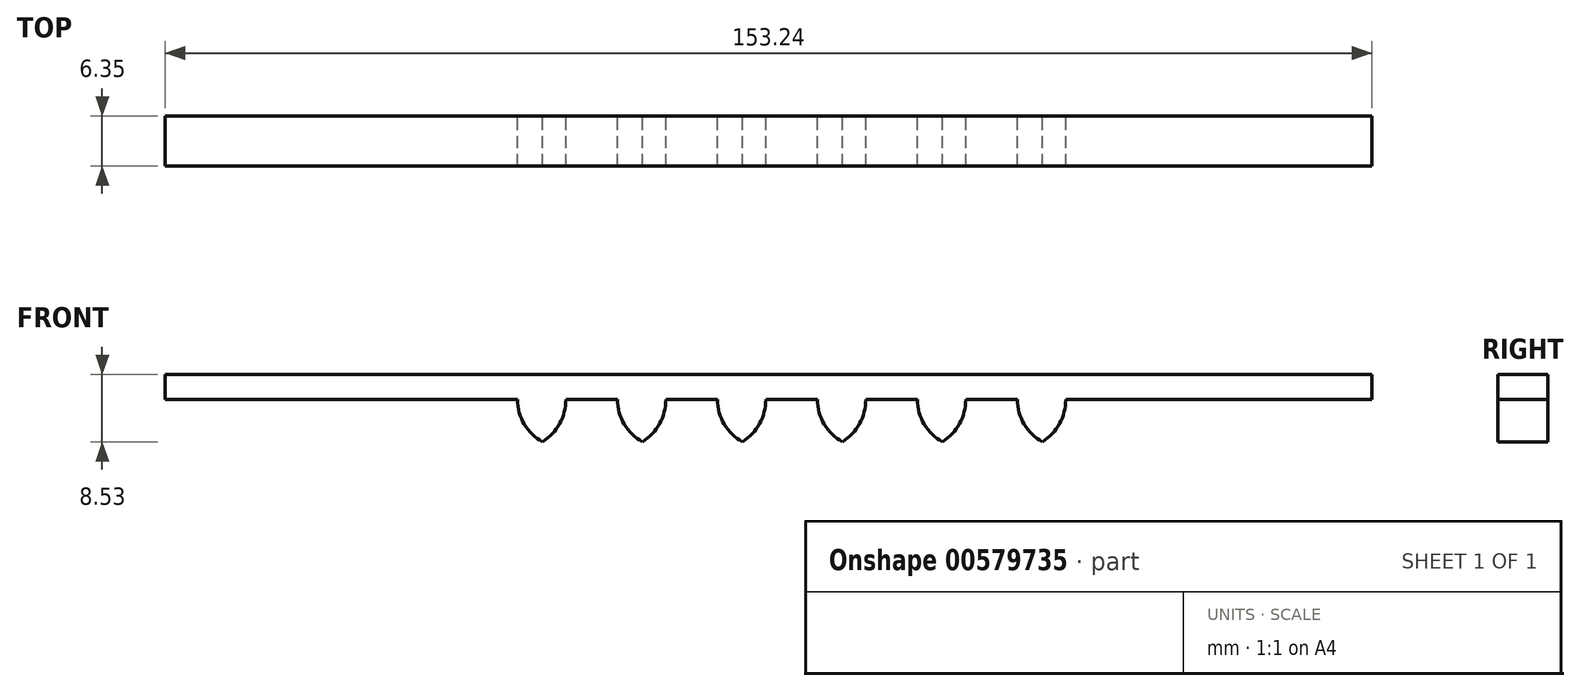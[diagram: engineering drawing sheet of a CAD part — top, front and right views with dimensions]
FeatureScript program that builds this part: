
annotation { "Feature Type Name" : "Feature", "Feature Type Description" : "" }
export const myFeature = defineFeature(function(context is Context, id is Id, definition is map)
    precondition{}
    {
        {
            var Q0;
            Q0=qCreatedBy(makeId("Front.planeOp"),FACE);
            var sketch = newSketch(context, id + "F0", { "sketchPlane" : qUnion([Q0])});
            skLineSegment(sketch, "E0.bottom", {"start": v(-100.17, 36.3) * mm, "end": v(-88.52, 36.3) * mm});
            skArc(sketch, "E1.1.0.0", {"start": v(-85.35, 30.93) * mm, "mid": v(-83.17, 33.23) * mm, "end": v(-82.38, 36.3) * mm});
            skArc(sketch, "E1.1.0.1", {"start": v(-88.52, 36.3) * mm, "mid": v(-87.67, 33.18) * mm, "end": v(-85.35, 30.93) * mm});
            skArc(sketch, "E1.3.0.0", {"start": v(-72.65, 30.93) * mm, "mid": v(-70.47, 33.23) * mm, "end": v(-69.68, 36.3) * mm});
            skArc(sketch, "E1.3.0.1", {"start": v(-75.82, 36.3) * mm, "mid": v(-74.97, 33.18) * mm, "end": v(-72.65, 30.93) * mm});
            skArc(sketch, "E1.5.0.0", {"start": v(-59.95, 30.93) * mm, "mid": v(-57.77, 33.23) * mm, "end": v(-56.98, 36.3) * mm});
            skArc(sketch, "E1.5.0.1", {"start": v(-63.12, 36.3) * mm, "mid": v(-62.27, 33.18) * mm, "end": v(-59.95, 30.93) * mm});
            skArc(sketch, "E1.7.0.0", {"start": v(-47.25, 30.93) * mm, "mid": v(-45.07, 33.23) * mm, "end": v(-44.28, 36.3) * mm});
            skArc(sketch, "E1.7.0.1", {"start": v(-50.42, 36.3) * mm, "mid": v(-49.57, 33.18) * mm, "end": v(-47.25, 30.93) * mm});
            skArc(sketch, "E1.9.0.0", {"start": v(-34.55, 30.93) * mm, "mid": v(-32.37, 33.23) * mm, "end": v(-31.58, 36.3) * mm});
            skArc(sketch, "E1.9.0.1", {"start": v(-37.72, 36.3) * mm, "mid": v(-36.87, 33.18) * mm, "end": v(-34.55, 30.93) * mm});
            skArc(sketch, "E1.11.0.0", {"start": v(-21.85, 30.93) * mm, "mid": v(-19.67, 33.23) * mm, "end": v(-18.88, 36.3) * mm});
            skArc(sketch, "E1.11.0.1", {"start": v(-25.02, 36.3) * mm, "mid": v(-24.17, 33.18) * mm, "end": v(-21.85, 30.93) * mm});
            skLineSegment(sketch, "E1.direction1", {"start": v(-91.7, 30.93) * mm, "end": v(-85.35, 30.93) * mm, "construction": true});
            skLineSegment(sketch, "E2.bottom", {"start": v(-107, 39.46) * mm, "end": v(1.43, 39.46) * mm});
            skLineSegment(sketch, "E3", {"start": v(-100.17, 36.3) * mm, "end": v(-117.13, 36.3) * mm});
            skLineSegment(sketch, "E4", {"start": v(-120.95, 39.46) * mm, "end": v(-107, 39.46) * mm});
            skLineSegment(sketch, "E5", {"start": v(1.43, 39.46) * mm, "end": v(6.42, 39.46) * mm});
            skLineSegment(sketch, "E6", {"start": v(-120.95, 39.46) * mm, "end": v(-133.26, 39.46) * mm});
            skLineSegment(sketch, "E7", {"start": v(-133.26, 39.46) * mm, "end": v(-133.26, 36.3) * mm});
            skLineSegment(sketch, "E8", {"start": v(-117.13, 36.3) * mm, "end": v(-127.73, 36.3) * mm});
            skLineSegment(sketch, "E9", {"start": v(19.98, 36.3) * mm, "end": v(19.98, 39.46) * mm});
            skLineSegment(sketch, "E10", {"start": v(19.98, 39.46) * mm, "end": v(19.98, 36.3) * mm});
            skLineSegment(sketch, "E11", {"start": v(6.42, 39.46) * mm, "end": v(19.98, 39.46) * mm});
            skLineSegment(sketch, "E12", {"start": v(1.43, 36.3) * mm, "end": v(15.68, 36.3) * mm});
            skLineSegment(sketch, "E13.trimOffspring", {"start": v(-82.38, 36.3) * mm, "end": v(-75.82, 36.3) * mm});
            skLineSegment(sketch, "E14.trimOffspring", {"start": v(-69.68, 36.3) * mm, "end": v(-63.12, 36.3) * mm});
            skLineSegment(sketch, "E15.trimOffspring", {"start": v(-56.98, 36.3) * mm, "end": v(-50.42, 36.3) * mm});
            skLineSegment(sketch, "E16.trimOffspring", {"start": v(-44.28, 36.3) * mm, "end": v(-37.72, 36.3) * mm});
            skLineSegment(sketch, "E17.trimOffspring", {"start": v(-31.58, 36.3) * mm, "end": v(-25.02, 36.3) * mm});
            skLineSegment(sketch, "E18.trimOffspring", {"start": v(-18.88, 36.3) * mm, "end": v(1.43, 36.3) * mm});
            skLineSegment(sketch, "E19", {"start": v(-127.73, 36.3) * mm, "end": v(-133.26, 36.3) * mm});
            skLineSegment(sketch, "E20", {"start": v(-133.26, 36.3) * mm, "end": v(19.98, 36.3) * mm});
            skArc(sketch, "E21", {"start": v(28.32, 23.56) * mm, "mid": v(28.4, 21.92) * mm, "end": v(28.6, 20.28) * mm});
            skArc(sketch, "E22", {"start": v(29.49, 30.12) * mm, "mid": v(26.05, 29.83) * mm, "end": v(23.22, 27.85) * mm});
            skArc(sketch, "E23", {"start": v(23.22, 27.85) * mm, "mid": v(25.2, 25.03) * mm, "end": v(28.32, 23.56) * mm});
            skArc(sketch, "E24.1.0", {"start": v(28.66, 20.3) * mm, "mid": v(25.83, 18.33) * mm, "end": v(24.37, 15.2) * mm});
            skArc(sketch, "E24.1.1", {"start": v(24.37, 15.2) * mm, "mid": v(27.5, 13.74) * mm, "end": v(30.93, 14.04) * mm});
            skArc(sketch, "E24.2.0", {"start": v(32.85, 11.38) * mm, "mid": v(31.39, 8.26) * mm, "end": v(31.68, 4.82) * mm});
            skArc(sketch, "E24.2.1", {"start": v(31.68, 4.82) * mm, "mid": v(35.12, 5.12) * mm, "end": v(37.95, 7.1) * mm});
            skArc(sketch, "E24.3.0", {"start": v(40.94, 5.75) * mm, "mid": v(41.24, 2.32) * mm, "end": v(43.21, -0.5) * mm});
            skArc(sketch, "E24.3.1", {"start": v(43.21, -0.5) * mm, "mid": v(46.04, 1.47) * mm, "end": v(47.5, 4.59) * mm});
            skArc(sketch, "E24.4.0", {"start": v(50.76, 4.92) * mm, "mid": v(52.74, 2.1) * mm, "end": v(55.86, 0.64) * mm});
            skArc(sketch, "E24.4.1", {"start": v(55.86, 0.64) * mm, "mid": v(57.32, 3.76) * mm, "end": v(57.02, 7.2) * mm});
            skArc(sketch, "E24.5.0", {"start": v(59.68, 9.12) * mm, "mid": v(62.8, 7.66) * mm, "end": v(66.24, 7.95) * mm});
            skArc(sketch, "E24.5.1", {"start": v(66.24, 7.95) * mm, "mid": v(65.94, 11.39) * mm, "end": v(63.97, 14.21) * mm});
            skArc(sketch, "E24.6.0", {"start": v(65.3, 17.2) * mm, "mid": v(65.32, 17.2) * mm, "end": v(65.33, 17.2) * mm});
            skPoint(sketch, "E24.center", {"position": v(47.4, 23.67) * mm});
            skPoint(sketch, "E24.11.0.end.orphan", {"position": v(28.56, 39.38) * mm});
            skPoint(sketch, "E24.10.0.end.orphan", {"position": v(38.94, 46.7) * mm});
            skPoint(sketch, "E25.orphan", {"position": v(71.57, 19.48) * mm});
            skArc(sketch, "E26.trimOffspring", {"start": v(30.88, 14.02) * mm, "mid": v(31.78, 12.62) * mm, "end": v(32.79, 11.3) * mm});
            skArc(sketch, "E27.trimOffspring", {"start": v(37.9, 7.04) * mm, "mid": v(39.38, 6.27) * mm, "end": v(40.92, 5.64) * mm});
            skArc(sketch, "E28.trimOffspring", {"start": v(47.49, 4.51) * mm, "mid": v(49.15, 4.6) * mm, "end": v(50.8, 4.82) * mm});
            skArc(sketch, "E29.trimOffspring", {"start": v(57.04, 7.15) * mm, "mid": v(58.43, 8.05) * mm, "end": v(59.74, 9.07) * mm});
            skArc(sketch, "E30.trimOffspring", {"start": v(63.97, 14.21) * mm, "mid": v(55.35, 40.86) * mm, "end": v(29.49, 30.12) * mm});
            skLineSegment(sketch, "E31.top", {"start": v(-105.22, 19.73) * mm, "end": v(-99.92, 19.73) * mm});
            skArc(sketch, "E32.MirrorCS", {"start": v(-99.92, 19.73) * mm, "mid": v(-99.07, 22.84) * mm, "end": v(-96.75, 25.1) * mm});
            skArc(sketch, "E33.MirrorCS", {"start": v(-96.75, 25.1) * mm, "mid": v(-94.58, 22.8) * mm, "end": v(-93.79, 19.73) * mm});
            skArc(sketch, "E34.MirrorCS", {"start": v(-87.22, 19.73) * mm, "mid": v(-86.37, 22.84) * mm, "end": v(-84.05, 25.1) * mm});
            skArc(sketch, "E35.MirrorCS", {"start": v(-84.05, 25.1) * mm, "mid": v(-81.88, 22.8) * mm, "end": v(-81.09, 19.73) * mm});
            skArc(sketch, "E36.MirrorCS", {"start": v(-74.52, 19.73) * mm, "mid": v(-73.67, 22.84) * mm, "end": v(-71.35, 25.1) * mm});
            skArc(sketch, "E37.MirrorCS", {"start": v(-71.35, 25.1) * mm, "mid": v(-69.18, 22.8) * mm, "end": v(-68.39, 19.73) * mm});
            skArc(sketch, "E38.MirrorCS", {"start": v(-61.82, 19.73) * mm, "mid": v(-60.97, 22.84) * mm, "end": v(-58.65, 25.1) * mm});
            skArc(sketch, "E39.MirrorCS", {"start": v(-58.65, 25.1) * mm, "mid": v(-56.48, 22.8) * mm, "end": v(-55.69, 19.73) * mm});
            skArc(sketch, "E40.MirrorCS", {"start": v(-49.12, 19.73) * mm, "mid": v(-48.27, 22.84) * mm, "end": v(-45.95, 25.1) * mm});
            skArc(sketch, "E41.MirrorCS", {"start": v(-45.95, 25.1) * mm, "mid": v(-43.78, 22.8) * mm, "end": v(-42.99, 19.73) * mm});
            skArc(sketch, "E42.MirrorCS", {"start": v(-36.42, 19.73) * mm, "mid": v(-35.57, 22.84) * mm, "end": v(-33.25, 25.1) * mm});
            skArc(sketch, "E43.MirrorCS", {"start": v(-33.25, 25.1) * mm, "mid": v(-31.08, 22.8) * mm, "end": v(-30.29, 19.73) * mm});
            skLineSegment(sketch, "E44.top", {"start": v(-112.05, 15.26) * mm, "end": v(-3.62, 15.26) * mm});
            skPoint(sketch, "E45.end.orphan", {"position": v(-93.79, 25.77) * mm});
            skPoint(sketch, "E46.end.orphan", {"position": v(-90.5, 19.73) * mm});
            skPoint(sketch, "E46.start.orphan", {"position": v(-90.5, 25.77) * mm});
            skPoint(sketch, "E47.start.orphan", {"position": v(-87.22, 25.77) * mm});
            skLineSegment(sketch, "E48", {"start": v(-112.05, 15.26) * mm, "end": v(-126, 15.26) * mm});
            skLineSegment(sketch, "E49", {"start": v(1.36, 15.26) * mm, "end": v(-3.62, 15.26) * mm});
            skLineSegment(sketch, "E50", {"start": v(-138.31, 15.26) * mm, "end": v(-126, 15.26) * mm});
            skLineSegment(sketch, "E51", {"start": v(14.93, 15.26) * mm, "end": v(1.36, 15.26) * mm});
            skLineSegment(sketch, "E52", {"start": v(10.63, 19.73) * mm, "end": v(-3.62, 19.73) * mm});
            skLineSegment(sketch, "E53.trimOffspring", {"start": v(-93.79, 19.73) * mm, "end": v(-87.22, 19.73) * mm});
            skLineSegment(sketch, "E54.trimOffspring", {"start": v(-81.09, 19.73) * mm, "end": v(-74.52, 19.73) * mm});
            skLineSegment(sketch, "E55.trimOffspring", {"start": v(-68.39, 19.73) * mm, "end": v(-61.82, 19.73) * mm});
            skLineSegment(sketch, "E56.trimOffspring", {"start": v(-55.69, 19.73) * mm, "end": v(-49.12, 19.73) * mm});
            skLineSegment(sketch, "E57.trimOffspring", {"start": v(-42.99, 19.73) * mm, "end": v(-36.42, 19.73) * mm});
            skLineSegment(sketch, "E58.trimOffspring", {"start": v(-30.29, 19.73) * mm, "end": v(-3.62, 19.73) * mm});
            skLineSegment(sketch, "E59", {"start": v(-132.78, 19.73) * mm, "end": v(-105.22, 19.73) * mm});
            skLineSegment(sketch, "E60", {"start": v(-132.78, 19.73) * mm, "end": v(-138.31, 19.73) * mm});
            skLineSegment(sketch, "E61", {"start": v(-138.31, 19.73) * mm, "end": v(14.93, 19.73) * mm});
            skLineSegment(sketch, "E62.trimOffspring", {"start": v(-138.31, 19.73) * mm, "end": v(-138.31, 15.26) * mm});
            skLineSegment(sketch, "E63.trimOffspring", {"start": v(14.93, 19.73) * mm, "end": v(14.93, 15.26) * mm});
            skSolve(sketch);
        }
        {
            var Q0;
            {var subQ30=sQuery(id+"F0.wireOp",EDGE,"E0.left");Q0=makeQuery(id+"F0.imprint","IMPRINT",FACE,{"disambiguationData":[TD([[makeQuery(id+"F0.imprint","IMPRINT",EDGE,{"derivedFrom":subQ30}),-1.0]])]});}
            var Q1;
            {var subQ0=sQuery(id+"F0.wireOp",EDGE,"I4CnsyD7-xhHb-1mGW-m4qb-hIhF2ATz1W8H");Q1=makeQuery(id+"F0.imprint","IMPRINT",FACE,{"disambiguationData":[TD([[makeQuery(id+"F0.imprint","IMPRINT",EDGE,{"derivedFrom":subQ0}),1.0]])]});}
            var Q2;
            {var subQ0=sQuery(id+"F0.wireOp",EDGE,"E1.1.0.0");Q2=makeQuery(id+"F0.imprint","IMPRINT",FACE,{"disambiguationData":[TD([[makeQuery(id+"F0.imprint","IMPRINT",EDGE,{"derivedFrom":subQ0}),1.0]])]});}
            var Q3;
            {var subQ0=sQuery(id+"F0.wireOp",EDGE,"E1.2.0.0");Q3=makeQuery(id+"F0.imprint","IMPRINT",FACE,{"disambiguationData":[TD([[makeQuery(id+"F0.imprint","IMPRINT",EDGE,{"derivedFrom":subQ0}),1.0]])]});}
            var Q4;
            {var subQ0=sQuery(id+"F0.wireOp",EDGE,"E1.3.0.0");Q4=makeQuery(id+"F0.imprint","IMPRINT",FACE,{"disambiguationData":[TD([[makeQuery(id+"F0.imprint","IMPRINT",EDGE,{"derivedFrom":subQ0}),1.0]])]});}
            var Q5;
            {var subQ0=sQuery(id+"F0.wireOp",EDGE,"E1.4.0.0");Q5=makeQuery(id+"F0.imprint","IMPRINT",FACE,{"disambiguationData":[TD([[makeQuery(id+"F0.imprint","IMPRINT",EDGE,{"derivedFrom":subQ0}),1.0]])]});}
            var Q6;
            {var subQ0=sQuery(id+"F0.wireOp",EDGE,"E1.5.0.0");Q6=makeQuery(id+"F0.imprint","IMPRINT",FACE,{"disambiguationData":[TD([[makeQuery(id+"F0.imprint","IMPRINT",EDGE,{"derivedFrom":subQ0}),1.0]])]});}
            var Q7;
            {var subQ0=sQuery(id+"F0.wireOp",EDGE,"E1.6.0.0");Q7=makeQuery(id+"F0.imprint","IMPRINT",FACE,{"disambiguationData":[TD([[makeQuery(id+"F0.imprint","IMPRINT",EDGE,{"derivedFrom":subQ0}),1.0]])]});}
            var Q8;
            {var subQ0=sQuery(id+"F0.wireOp",EDGE,"E1.7.0.0");Q8=makeQuery(id+"F0.imprint","IMPRINT",FACE,{"disambiguationData":[TD([[makeQuery(id+"F0.imprint","IMPRINT",EDGE,{"derivedFrom":subQ0}),1.0]])]});}
            var Q9;
            {var subQ0=sQuery(id+"F0.wireOp",EDGE,"E1.8.0.0");Q9=makeQuery(id+"F0.imprint","IMPRINT",FACE,{"disambiguationData":[TD([[makeQuery(id+"F0.imprint","IMPRINT",EDGE,{"derivedFrom":subQ0}),1.0]])]});}
            var Q10;
            {var subQ0=sQuery(id+"F0.wireOp",EDGE,"E1.9.0.0");Q10=makeQuery(id+"F0.imprint","IMPRINT",FACE,{"disambiguationData":[TD([[makeQuery(id+"F0.imprint","IMPRINT",EDGE,{"derivedFrom":subQ0}),1.0]])]});}
            var Q11;
            {var subQ0=sQuery(id+"F0.wireOp",EDGE,"E1.10.0.0");Q11=makeQuery(id+"F0.imprint","IMPRINT",FACE,{"disambiguationData":[TD([[makeQuery(id+"F0.imprint","IMPRINT",EDGE,{"derivedFrom":subQ0}),1.0]])]});}
            var Q12;
            {var subQ0=sQuery(id+"F0.wireOp",EDGE,"E1.11.0.0");Q12=makeQuery(id+"F0.imprint","IMPRINT",FACE,{"disambiguationData":[TD([[makeQuery(id+"F0.imprint","IMPRINT",EDGE,{"derivedFrom":subQ0}),1.0]])]});}
            var Q13;
            {var subQ0=sQuery(id+"F0.wireOp",EDGE,"E1.12.0.0");Q13=makeQuery(id+"F0.imprint","IMPRINT",FACE,{"disambiguationData":[TD([[makeQuery(id+"F0.imprint","IMPRINT",EDGE,{"derivedFrom":subQ0}),1.0]])]});}
            var Q14;
            {var subQ0=sQuery(id+"F0.wireOp",EDGE,"E1.13.0.0");Q14=makeQuery(id+"F0.imprint","IMPRINT",FACE,{"disambiguationData":[TD([[makeQuery(id+"F0.imprint","IMPRINT",EDGE,{"derivedFrom":subQ0}),1.0]])]});}
            var Q15;
            {var subQ0=sQuery(id+"F0.wireOp",EDGE,"E1.14.0.0");Q15=makeQuery(id+"F0.imprint","IMPRINT",FACE,{"disambiguationData":[TD([[makeQuery(id+"F0.imprint","IMPRINT",EDGE,{"derivedFrom":subQ0}),1.0]])]});}
            var Q16;
            {var subQ0=sQuery(id+"F0.wireOp",EDGE,"E1.15.0.0");Q16=makeQuery(id+"F0.imprint","IMPRINT",FACE,{"disambiguationData":[TD([[makeQuery(id+"F0.imprint","IMPRINT",EDGE,{"derivedFrom":subQ0}),1.0]])]});}
            var Q17;
            {var subQ0=sQuery(id+"F0.wireOp",EDGE,"d1ebb186-b781-4031-9433-506903d14f690.MirrorCS");Q17=makeQuery(id+"F0.imprint","IMPRINT",FACE,{"disambiguationData":[TD([[makeQuery(id+"F0.imprint","IMPRINT",EDGE,{"derivedFrom":subQ0}),-1.0]])]});}
            var Q18;
            {var subQ0=sQuery(id+"F0.wireOp",EDGE,"d048a6cf-c931-42d6-915b-dd91fbb8fda30.MirrorCS");Q18=makeQuery(id+"F0.imprint","IMPRINT",FACE,{"disambiguationData":[TD([[makeQuery(id+"F0.imprint","IMPRINT",EDGE,{"derivedFrom":subQ0}),-1.0]])]});}
            var Q19;
            {var subQ0=sQuery(id+"F0.wireOp",EDGE,"bdc9a796-f07d-4989-ac5a-d5d73a7a29dd0.MirrorCS");Q19=makeQuery(id+"F0.imprint","IMPRINT",FACE,{"disambiguationData":[TD([[makeQuery(id+"F0.imprint","IMPRINT",EDGE,{"derivedFrom":subQ0}),-1.0]])]});}
            var Q20;
            {var subQ0=sQuery(id+"F0.wireOp",EDGE,"e91bf60a-8a31-477d-9e45-87d6053abe480.MirrorCS");Q20=makeQuery(id+"F0.imprint","IMPRINT",FACE,{"disambiguationData":[TD([[makeQuery(id+"F0.imprint","IMPRINT",EDGE,{"derivedFrom":subQ0}),-1.0]])]});}
            var Q21;
            {var subQ0=sQuery(id+"F0.wireOp",EDGE,"50d5f359-82e2-4939-bb1e-8d76c203bae80.MirrorCS");Q21=makeQuery(id+"F0.imprint","IMPRINT",FACE,{"disambiguationData":[TD([[makeQuery(id+"F0.imprint","IMPRINT",EDGE,{"derivedFrom":subQ0}),-1.0]])]});}
            var Q22;
            {var subQ0=sQuery(id+"F0.wireOp",EDGE,"f000155d-3a27-43ec-8001-4f9902a59fb40.MirrorCS");Q22=makeQuery(id+"F0.imprint","IMPRINT",FACE,{"disambiguationData":[TD([[makeQuery(id+"F0.imprint","IMPRINT",EDGE,{"derivedFrom":subQ0}),-1.0]])]});}
            var Q23;
            {var subQ0=sQuery(id+"F0.wireOp",EDGE,"8c738a82-8504-453a-a8cb-555aae9655c40.MirrorCS");Q23=makeQuery(id+"F0.imprint","IMPRINT",FACE,{"disambiguationData":[TD([[makeQuery(id+"F0.imprint","IMPRINT",EDGE,{"derivedFrom":subQ0}),-1.0]])]});}
            var Q24;
            {var subQ0=sQuery(id+"F0.wireOp",EDGE,"1a87cf0a-5dec-4e1e-9c7a-696ee766e6280.MirrorCS");Q24=makeQuery(id+"F0.imprint","IMPRINT",FACE,{"disambiguationData":[TD([[makeQuery(id+"F0.imprint","IMPRINT",EDGE,{"derivedFrom":subQ0}),-1.0]])]});}
            var Q25;
            {var subQ0=sQuery(id+"F0.wireOp",EDGE,"286fcfac-c6ca-404a-82a1-fe164d7bc4fc0.MirrorCS");Q25=makeQuery(id+"F0.imprint","IMPRINT",FACE,{"disambiguationData":[TD([[makeQuery(id+"F0.imprint","IMPRINT",EDGE,{"derivedFrom":subQ0}),-1.0]])]});}
            var Q26;
            {var subQ0=sQuery(id+"F0.wireOp",EDGE,"311bcf0f-cd40-487c-ba07-012c7cee469a0.MirrorCS");Q26=makeQuery(id+"F0.imprint","IMPRINT",FACE,{"disambiguationData":[TD([[makeQuery(id+"F0.imprint","IMPRINT",EDGE,{"derivedFrom":subQ0}),-1.0]])]});}
            var Q27;
            {var subQ0=sQuery(id+"F0.wireOp",EDGE,"e6eba2f3-02d5-462b-abb4-43e06cf37dd00.MirrorCS");Q27=makeQuery(id+"F0.imprint","IMPRINT",FACE,{"disambiguationData":[TD([[makeQuery(id+"F0.imprint","IMPRINT",EDGE,{"derivedFrom":subQ0}),-1.0]])]});}
            var Q28;
            {var subQ0=sQuery(id+"F0.wireOp",EDGE,"a5eb41cc-492e-4858-8f34-e71dc105c88e0.MirrorCS");Q28=makeQuery(id+"F0.imprint","IMPRINT",FACE,{"disambiguationData":[TD([[makeQuery(id+"F0.imprint","IMPRINT",EDGE,{"derivedFrom":subQ0}),-1.0]])]});}
            var Q29;
            {var subQ0=sQuery(id+"F0.wireOp",EDGE,"1f745a6e-db67-4c08-b781-e359b20177ff0.MirrorCS");Q29=makeQuery(id+"F0.imprint","IMPRINT",FACE,{"disambiguationData":[TD([[makeQuery(id+"F0.imprint","IMPRINT",EDGE,{"derivedFrom":subQ0}),-1.0]])]});}
            var Q30;
            {var subQ0=sQuery(id+"F0.wireOp",EDGE,"5a0744fe-8fe7-4ce7-aec0-d37810d535d30.MirrorCS");Q30=makeQuery(id+"F0.imprint","IMPRINT",FACE,{"disambiguationData":[TD([[makeQuery(id+"F0.imprint","IMPRINT",EDGE,{"derivedFrom":subQ0}),-1.0]])]});}
            var Q31;
            {var subQ0=sQuery(id+"F0.wireOp",EDGE,"546d33ef-39f9-4c82-b962-d1ea12a8f4dd0.MirrorCS");Q31=makeQuery(id+"F0.imprint","IMPRINT",FACE,{"disambiguationData":[TD([[makeQuery(id+"F0.imprint","IMPRINT",EDGE,{"derivedFrom":subQ0}),-1.0]])]});}
            var Q32;
            {var subQ0=sQuery(id+"F0.wireOp",EDGE,"5b461c2d-675d-4389-a142-29c418c11a020.MirrorCS");Q32=makeQuery(id+"F0.imprint","IMPRINT",FACE,{"disambiguationData":[TD([[makeQuery(id+"F0.imprint","IMPRINT",EDGE,{"derivedFrom":subQ0}),-1.0]])]});}
            var Q33;
            Q33=makeQuery(id+"F0.imprint","IMPRINT",FACE,{"disambiguationData":[TD([[makeQuery(id+"F0.imprint","IMPRINT",EDGE,{"derivedFrom":sQuery(id+"F0.wireOp",EDGE,"E2.bottom")}),-1.0]])]});
            var Q34;
            Q34=makeQuery(id+"F0.imprint","IMPRINT",FACE,{"disambiguationData":[TD([[makeQuery(id+"F0.imprint","IMPRINT",EDGE,{"derivedFrom":sQuery(id+"F0.wireOp",EDGE,"E2.top")}),1.0]])]});
            extrude(context, id + "F1", {"entities" : qUnion([Q0, Q1, Q2, Q3, Q4, Q5, Q6, Q7, Q8, Q9, Q10, Q11, Q12, Q13, Q14, Q15, Q16, Q17, Q18, Q19, Q20, Q21, Q22, Q23, Q24, Q25, Q26, Q27, Q28, Q29, Q30, Q31, Q32, Q33, Q34]), "depth" : 6.35 * mm, "offsetDistance" : 25.4 * mm});
        }
    });
